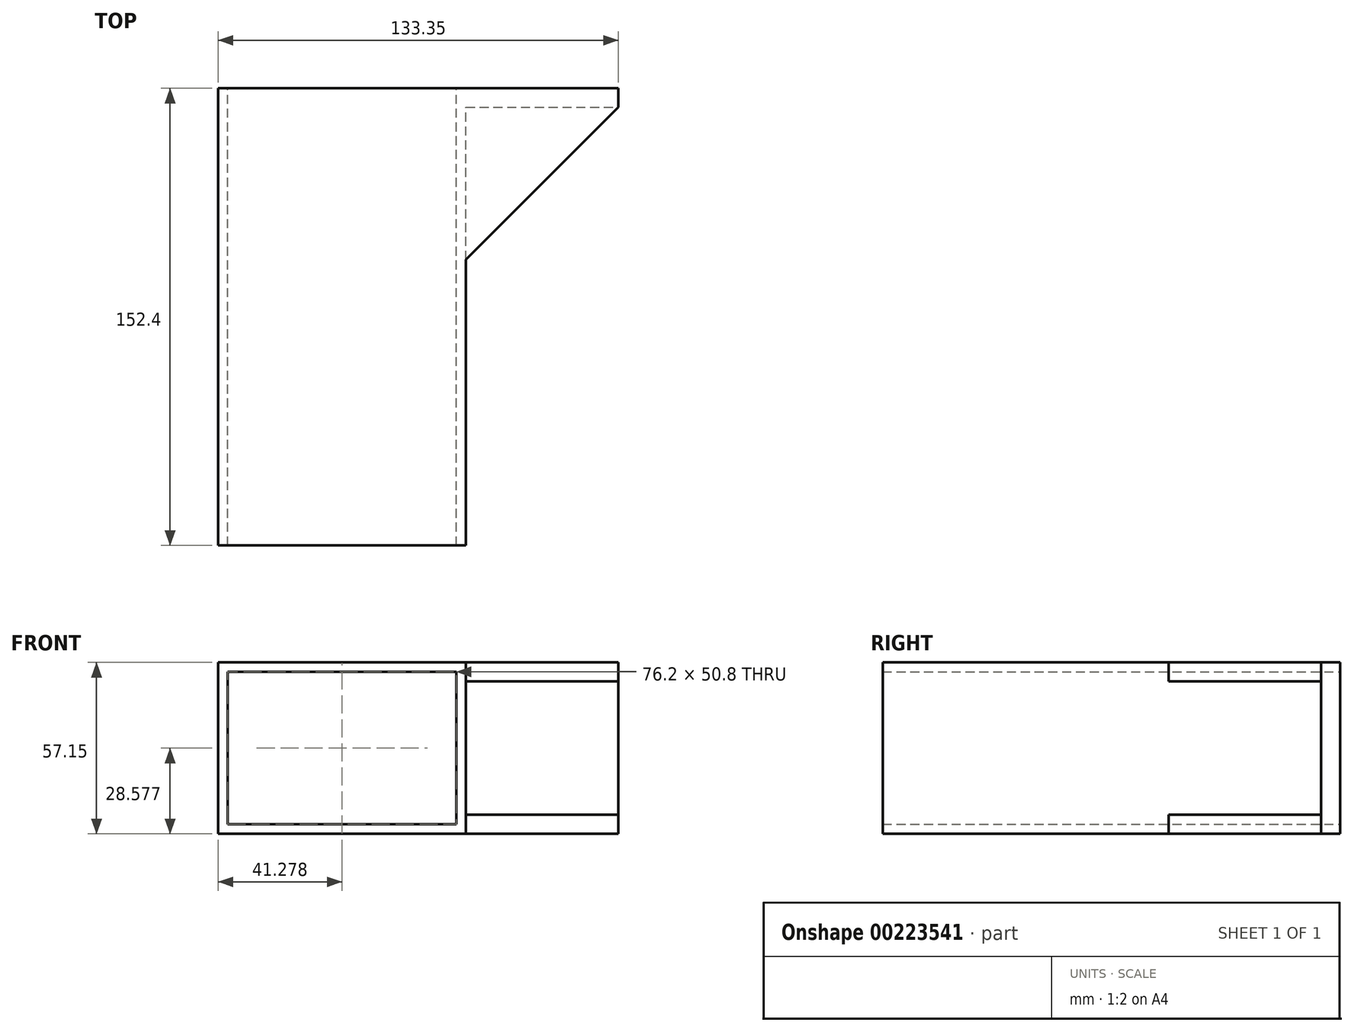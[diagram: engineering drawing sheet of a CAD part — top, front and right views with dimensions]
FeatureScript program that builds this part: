
annotation { "Feature Type Name" : "Feature", "Feature Type Description" : "" }
export const myFeature = defineFeature(function(context is Context, id is Id, definition is map)
    precondition{}
    {
        {
            var Q0;
            Q0=qCreatedBy(makeId("Front.planeOp"),FACE);
            var sketch = newSketch(context, id + "F0", { "sketchPlane" : qUnion([Q0])});
            skLineSegment(sketch, "E0.bottom", {"start": v(-34.37, 6.03) * mm, "end": v(41.83, 6.03) * mm});
            skLineSegment(sketch, "E0.top", {"start": v(-34.37, -44.77) * mm, "end": v(41.83, -44.77) * mm});
            skLineSegment(sketch, "E0.left", {"start": v(-34.37, 6.03) * mm, "end": v(-34.37, -44.77) * mm});
            skLineSegment(sketch, "E0.right", {"start": v(41.83, 6.03) * mm, "end": v(41.83, -44.77) * mm});
            skLineSegment(sketch, "E1.0", {"start": v(-37.55, 9.2) * mm, "end": v(45, 9.2) * mm});
            skLineSegment(sketch, "E1.1", {"start": v(-37.55, 9.2) * mm, "end": v(-37.55, -47.95) * mm});
            skLineSegment(sketch, "E1.2", {"start": v(-37.55, -47.95) * mm, "end": v(45, -47.95) * mm});
            skLineSegment(sketch, "E1.3", {"start": v(45, 9.2) * mm, "end": v(45, -47.95) * mm});
            skSolve(sketch);
        }
        {
            var Q0;
            Q0=makeQuery(id+"F0.imprint","IMPRINT",FACE,{"disambiguationData":[TD([[makeQuery(id+"F0.imprint","IMPRINT",EDGE,{"derivedFrom":sQuery(id+"F0.wireOp",EDGE,"E0.bottom")}),1.0]])]});
            extrude(context, id + "F1", {"entities" : qUnion([Q0]), "depth" : 152.4 * mm});
        }
        {
            var Q0;
            Q0=makeQuery(id+"F1.opExtrude","SWEPT_FACE",FACE,{"disambiguationData":[OSD([sQuery(id+"F0.wireOp",EDGE,"E1.3")])]});
            var sketch = newSketch(context, id + "F2", { "sketchPlane" : qUnion([Q0])});
            skLineSegment(sketch, "E2.bottom", {"start": v(0, 9.2) * mm, "end": v(-6.35, 9.2) * mm});
            skLineSegment(sketch, "E2.top", {"start": v(0, -47.95) * mm, "end": v(-6.35, -47.95) * mm});
            skLineSegment(sketch, "E2.left", {"start": v(0, 9.2) * mm, "end": v(0, -47.95) * mm});
            skLineSegment(sketch, "E2.right", {"start": v(-6.35, 9.2) * mm, "end": v(-6.35, -47.95) * mm});
            skSolve(sketch);
        }
        {
            var Q0;
            Q0=qSketchRegion(id+"F2",true);
            extrude(context, id + "F3", {"entities" : qUnion([Q0]), "operationType" : NewBodyOperationType.ADD, "depth" : 50.8 * mm});
        }
        {
            var Q0;
            Q0=makeQuery(id+"F3.opExtrude","SWEPT_FACE",FACE,{"disambiguationData":[OSD([sQuery(id+"F2.wireOp",EDGE,"E2.right")])]});
            var sketch = newSketch(context, id + "F4", { "sketchPlane" : qUnion([Q0])});
            skLineSegment(sketch, "E3.bottom", {"start": v(45, -47.95) * mm, "end": v(95.8, -47.95) * mm});
            skLineSegment(sketch, "E3.top", {"start": v(45, -41.6) * mm, "end": v(95.8, -41.6) * mm});
            skLineSegment(sketch, "E3.left", {"start": v(45, -47.95) * mm, "end": v(45, -41.6) * mm});
            skLineSegment(sketch, "E3.right", {"start": v(95.8, -47.95) * mm, "end": v(95.8, -41.6) * mm});
            skLineSegment(sketch, "E4.bottom", {"start": v(95.8, 9.2) * mm, "end": v(45, 9.2) * mm});
            skLineSegment(sketch, "E4.top", {"start": v(95.8, 2.85) * mm, "end": v(45, 2.85) * mm});
            skLineSegment(sketch, "E4.left", {"start": v(95.8, 9.2) * mm, "end": v(95.8, 2.85) * mm});
            skLineSegment(sketch, "E4.right", {"start": v(45, 9.2) * mm, "end": v(45, 2.85) * mm});
            skSolve(sketch);
        }
        {
            var Q0;
            Q0=qSketchRegion(id+"F4",true);
            extrude(context, id + "F5", {"entities" : qUnion([Q0]), "operationType" : NewBodyOperationType.ADD, "depth" : 50.8 * mm});
        }
        {
            var Q0;
            Q0=makeQuery(id+"F5.boolean.opBoolean","MERGE",FACE,{"derivedFrom":[makeQuery(id+"F3.boolean.opBoolean","MERGE",FACE,{"derivedFrom":[makeQuery(id+"F1.opExtrude","SWEPT_FACE",FACE,{"disambiguationData":[OSD([sQuery(id+"F0.wireOp",EDGE,"E1.0")])]}),makeQuery(id+"F3.opExtrude","SWEPT_FACE",FACE,{"disambiguationData":[OSD([sQuery(id+"F2.wireOp",EDGE,"E2.bottom")])]})]}),makeQuery(id+"F5.opExtrude","SWEPT_FACE",FACE,{"disambiguationData":[OSD([sQuery(id+"F4.wireOp",EDGE,"E4.bottom")])]})]});
            var sketch = newSketch(context, id + "F6", { "sketchPlane" : qUnion([Q0])});
            skLineSegment(sketch, "E5", {"start": v(45, -57.15) * mm, "end": v(95.8, -6.35) * mm});
            skLineSegment(sketch, "E6", {"start": v(45, -57.15) * mm, "end": v(95.8, -57.15) * mm});
            skLineSegment(sketch, "E7", {"start": v(95.8, -57.15) * mm, "end": v(95.8, -6.35) * mm});
            skSolve(sketch);
        }
        {
            var Q0;
            Q0=qSketchRegion(id+"F6",true);
            extrude(context, id + "F7", {"entities" : qUnion([Q0]), "operationType" : NewBodyOperationType.REMOVE, "oppositeDirection" : true, "depth" : 118.62 * mm});
        }
    });
